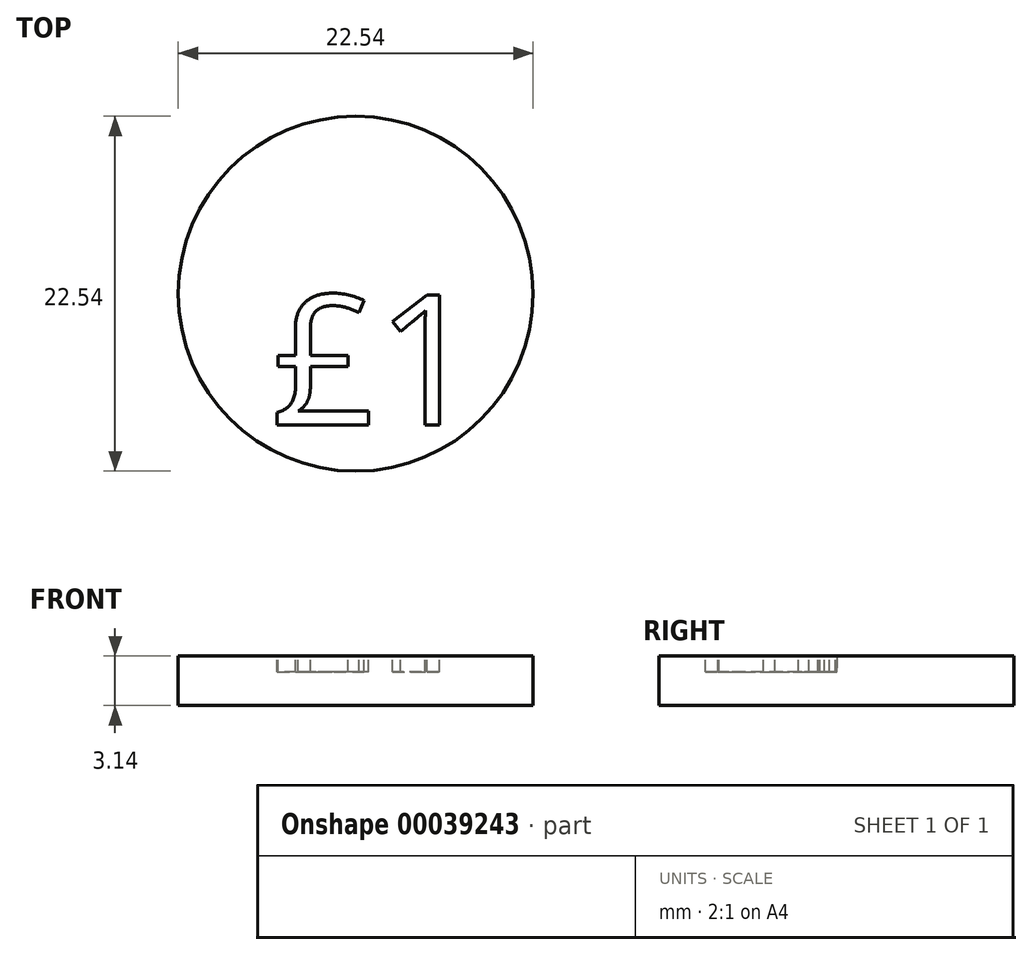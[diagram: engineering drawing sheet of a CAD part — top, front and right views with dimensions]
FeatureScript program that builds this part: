
annotation { "Feature Type Name" : "Feature", "Feature Type Description" : "" }
export const myFeature = defineFeature(function(context is Context, id is Id, definition is map)
    precondition{}
    {
        {
            var Q0;
            Q0=qCreatedBy(makeId("Top.planeOp"),FACE);
            var sketch = newSketch(context, id + "F0", { "sketchPlane" : qUnion([Q0])});
            skCircle(sketch, "E0", {"center": v(0, 0) * mm, "radius": 11.27 * mm});
            skSolve(sketch);
        }
        {
            var Q0;
            Q0 = qSketchRegion(id + "F0", true);
            extrude(context, id + "F1", {"entities" : qUnion([Q0]), "depth" : 3.14 * mm});
        }
        {
            var Q0;
            Q0=makeQuery(id+"F1.opExtrude","CAP_FACE",FACE,{"disambiguationData":[OSD([sQuery(id+"F0.wireOp",EDGE,"E0"),sQuery(id+"F0.wireOp",EDGE,"b1e43adf-e12e-4730-8375-2b69b1993464")])],"isStart":false});
            var sketch = newSketch(context, id + "F2", { "sketchPlane" : qUnion([Q0])});
            skText(sketch, "E1", { "text": "£1", "fontName": "OpenSans-Regular.ttf"});
            const initialGuessF2  = {"E1": [-0.00534, -0.00833, 1, 0, 0.00833]};
            skSetInitialGuess(sketch, initialGuessF2);
            skSolve(sketch);
        }
        {
            var Q0;
            Q0 = qSketchRegion(id + "F2", true);
            extrude(context, id + "F3", {"entities" : qUnion([Q0]), "operationType" : NewBodyOperationType.REMOVE, "oppositeDirection" : true, "depth" : 1 * mm});
        }
    });
